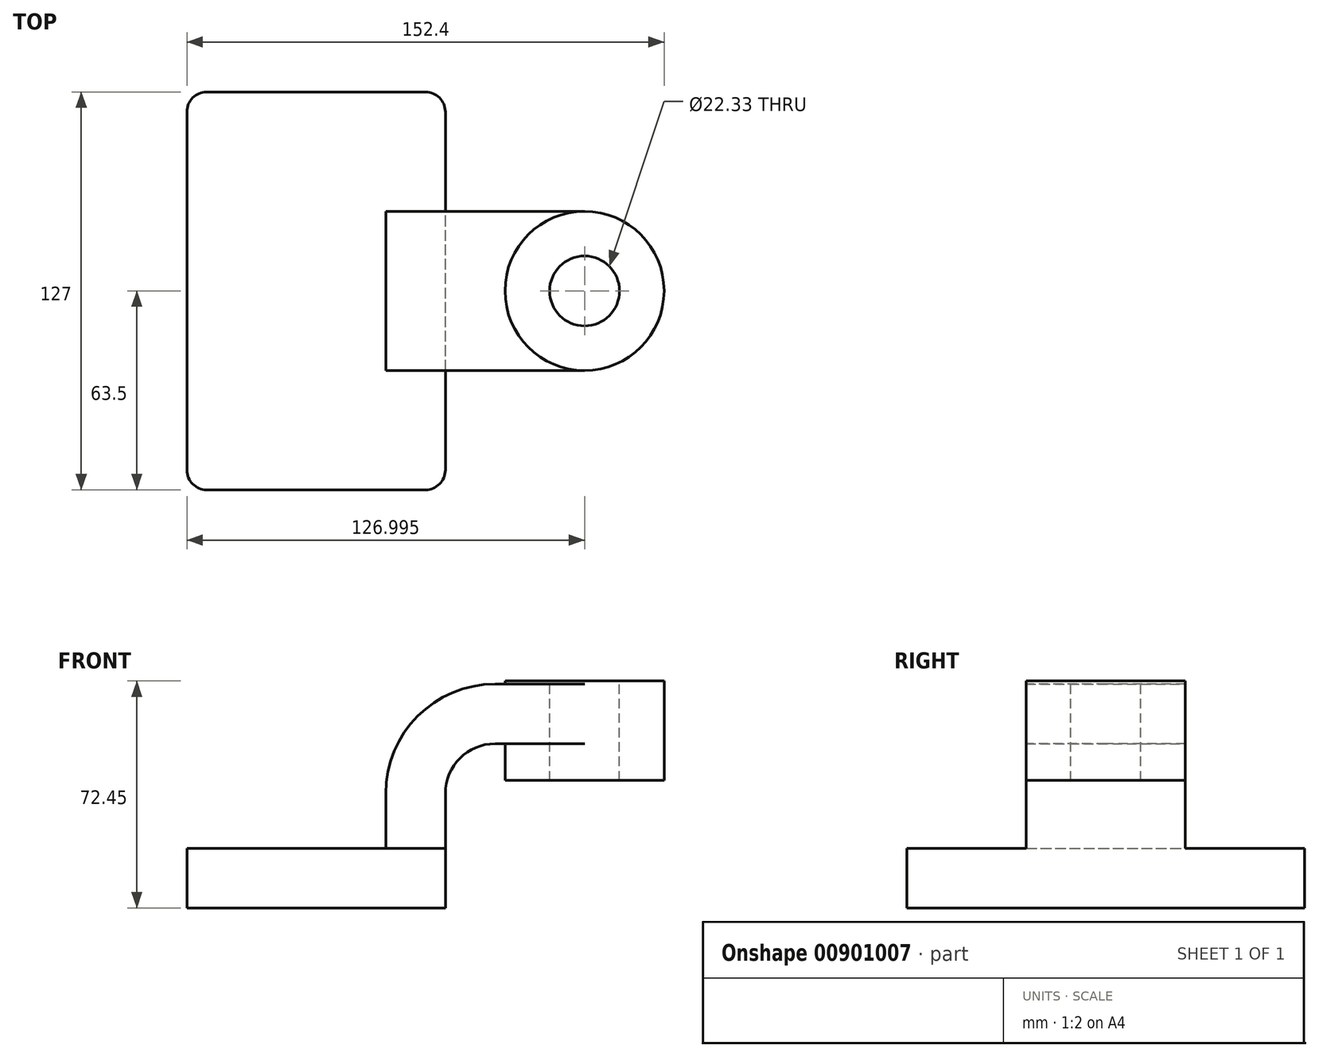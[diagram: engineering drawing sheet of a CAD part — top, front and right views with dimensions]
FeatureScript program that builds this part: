
annotation { "Feature Type Name" : "Feature", "Feature Type Description" : "" }
export const myFeature = defineFeature(function(context is Context, id is Id, definition is map)
    precondition{}
    {
        {
            var Q0;
            Q0=qCreatedBy(makeId("Front.planeOp"),FACE);
            var sketch = newSketch(context, id + "F0", { "sketchPlane" : qUnion([Q0])});
            skLineSegment(sketch, "E0.bottom", {"start": v(-41.28, 9.52) * mm, "end": v(41.27, 9.53) * mm});
            skLineSegment(sketch, "E0.top", {"start": v(-41.28, -9.53) * mm, "end": v(41.28, -9.53) * mm});
            skLineSegment(sketch, "E0.left", {"start": v(-41.28, 9.52) * mm, "end": v(-41.28, -9.53) * mm});
            skLineSegment(sketch, "E0.right", {"start": v(41.27, 9.53) * mm, "end": v(41.28, -9.52) * mm});
            skPoint(sketch, "E0.middle", {"position": v(0, 0) * mm});
            skLineSegment(sketch, "E1.bottom", {"start": v(111.13, 31.17) * mm, "end": v(60.33, 31.17) * mm});
            skLineSegment(sketch, "E1.top", {"start": v(111.13, 62.92) * mm, "end": v(60.33, 62.92) * mm});
            skLineSegment(sketch, "E1.left", {"start": v(111.13, 31.17) * mm, "end": v(111.13, 62.92) * mm});
            skLineSegment(sketch, "E1.right", {"start": v(60.33, 31.17) * mm, "end": v(60.33, 62.92) * mm});
            skPoint(sketch, "E1.middle", {"position": v(85.73, 47.04) * mm});
            skLineSegment(sketch, "E2", {"start": v(41.27, 9.53) * mm, "end": v(41.27, 27) * mm});
            skArc(sketch, "E3", {"start": v(41.27, 27) * mm, "mid": v(45.92, 38.23) * mm, "end": v(57.15, 42.88) * mm});
            skLineSegment(sketch, "E4", {"start": v(57.15, 42.88) * mm, "end": v(85.73, 42.88) * mm});
            skLineSegment(sketch, "E5.0", {"start": v(57.15, 61.93) * mm, "end": v(85.73, 61.93) * mm});
            skArc(sketch, "E5.1", {"start": v(22.22, 27) * mm, "mid": v(32.45, 51.7) * mm, "end": v(57.15, 61.93) * mm});
            skLineSegment(sketch, "E5.2", {"start": v(22.23, 9.53) * mm, "end": v(22.23, 27) * mm});
            skLineSegment(sketch, "E6", {"start": v(85.73, 31.17) * mm, "end": v(85.73, 62.92) * mm});
            skFitSpline(sketch, "E7", {"points": [v(-41.28, 9.52) * mm, v(57.15, 61.93) * mm], "startDerivative": vector(0, 106.86) * mm, "endDerivative": vector(146.35, -0.54) * mm});
            skSolve(sketch);
        }
        {
            var Q0;
            Q0=makeQuery(id+"F0.imprint","IMPRINT",FACE,{"disambiguationData":[TD([[makeQuery(id+"F0.imprint","IMPRINT",EDGE,{"derivedFrom":sQuery(id+"F0.wireOp",EDGE,"E0.top")}),1.0]])]});
            extrude(context, id + "F1", {"entities" : qUnion([Q0]), "endBound" : BoundingType.SYMMETRIC, "depth" : 127 * mm, "offsetDistance" : 25 * mm});
        }
        {
            var Q0;
            {var subQ1=sQuery(id+"F0.wireOp",EDGE,"E2");Q0=makeQuery(id+"F0.imprint","IMPRINT",FACE,{"disambiguationData":[TD([[makeQuery(id+"F0.imprint","IMPRINT",EDGE,{"derivedFrom":subQ1}),1.0]])]});}
            var Q1;
            {var subQ0=sQuery(id+"F0.wireOp",EDGE,"E4");var subQ1=sQuery(id+"F0.wireOp",EDGE,"E1.right");var subQ2=makeQuery(id+"F0.imprint","INTERSECT",VERTEX,{"derivedFrom":[subQ1,subQ0]});Q1=makeQuery(id+"F0.imprint","IMPRINT",FACE,{"disambiguationData":[TD([[makeQuery(id+"F0.imprint","IMPRINT",EDGE,{"disambiguationData":[TD([[subQ2,-1.0]])],"derivedFrom":subQ1}),-1.0]])]});}
            extrude(context, id + "F2", {"entities" : qUnion([Q0, Q1]), "operationType" : NewBodyOperationType.ADD, "endBound" : BoundingType.SYMMETRIC, "depth" : 50.8 * mm, "offsetDistance" : 25 * mm});
        }
        {
            var Q0;
            Q0=makeQuery(id+"F0.imprint","IMPRINT",FACE,{"disambiguationData":[TD([[makeQuery(id+"F0.imprint","IMPRINT",EDGE,{"derivedFrom":sQuery(id+"F0.wireOp",EDGE,"E5.1")}),1.0]])]});
            extrude(context, id + "F3", {"entities" : qUnion([Q0]), "operationType" : NewBodyOperationType.ADD, "endBound" : BoundingType.SYMMETRIC, "depth" : 15.88 * mm, "offsetDistance" : 25 * mm});
        }
        {
            var Q0;
            {var subQ4=sQuery(id+"F0.wireOp",EDGE,"E1.left");Q0=makeQuery(id+"F0.imprint","IMPRINT",FACE,{"disambiguationData":[TD([[makeQuery(id+"F0.imprint","IMPRINT",EDGE,{"derivedFrom":subQ4}),1.0]])]});}
            var Q1;
            Q1=sQuery(id+"F0.wireOp",EDGE,"E6");
            revolve(context, id + "F4", {"operationType" : NewBodyOperationType.ADD, "surfaceOperationType" : NewSurfaceOperationType.NEW, "entities" : qUnion([Q0]), "axis" : qUnion([Q1]), "revolveType" : RevolveType.FULL});
        }
        {
            var Q0;
            Q0=makeQuery(id+"F1.opExtrude","CAP_EDGE",EDGE,{"disambiguationData":[OSD([sQuery(id+"F0.wireOp",EDGE,"E0.right")])],"isStart":true});
            var Q1;
            Q1=makeQuery(id+"F1.opExtrude","CAP_EDGE",EDGE,{"disambiguationData":[OSD([sQuery(id+"F0.wireOp",EDGE,"E0.left")])],"isStart":true});
            var Q2;
            Q2=makeQuery(id+"F1.opExtrude","CAP_EDGE",EDGE,{"disambiguationData":[OSD([sQuery(id+"F0.wireOp",EDGE,"E0.left")])],"isStart":false});
            var Q3;
            Q3=makeQuery(id+"F1.opExtrude","CAP_EDGE",EDGE,{"disambiguationData":[OSD([sQuery(id+"F0.wireOp",EDGE,"E0.right")])],"isStart":false});
            fillet(context, id + "F5", {"entities" : qUnion([Q0, Q1, Q2, Q3]), "radius" : 6.35 * mm, "tangentPropagation" : true, "allowEdgeOverflow" : false});
        }
        {
            var Q0;
            Q0=makeQuery(id+"F4.opRevolve","SWEPT_FACE",FACE,{"disambiguationData":[OSD([sQuery(id+"F0.wireOp",EDGE,"E1.top")])]});
            var sketch = newSketch(context, id + "F6", { "sketchPlane" : qUnion([Q0])});
            skCircle(sketch, "E8", {"center": v(85.73, 0) * mm, "radius": 11.16 * mm});
            skSolve(sketch);
        }
        {
            var Q0;
            Q0 = qSketchRegion(id + "F6", true);
            extrude(context, id + "F7", {"entities" : qUnion([Q0]), "operationType" : NewBodyOperationType.REMOVE, "oppositeDirection" : true, "depth" : 35 * mm, "offsetDistance" : 25 * mm});
        }
    });
